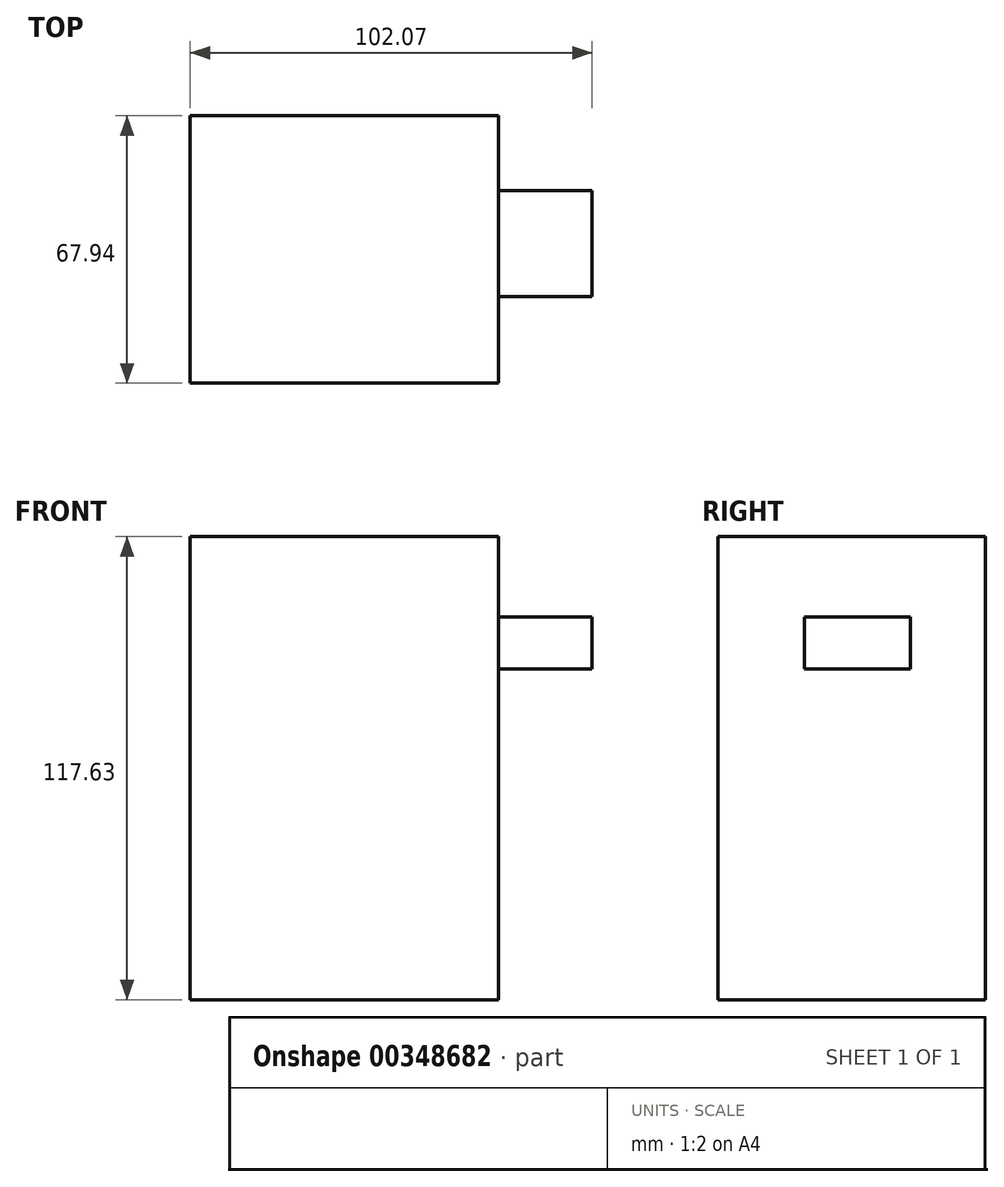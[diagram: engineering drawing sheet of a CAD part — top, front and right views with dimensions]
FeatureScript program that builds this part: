
annotation { "Feature Type Name" : "Feature", "Feature Type Description" : "" }
export const myFeature = defineFeature(function(context is Context, id is Id, definition is map)
    precondition{}
    {
        {
            var Q0;
            Q0=qCreatedBy(makeId("Top.planeOp"),FACE);
            var sketch = newSketch(context, id + "F0", { "sketchPlane" : qUnion([Q0])});
            skLineSegment(sketch, "E0.bottom", {"start": v(39.18, 45.93) * mm, "end": v(-39.18, 45.93) * mm});
            skLineSegment(sketch, "E0.top", {"start": v(39.18, -22.01) * mm, "end": v(-39.18, -22.01) * mm});
            skLineSegment(sketch, "E0.left", {"start": v(39.18, 45.93) * mm, "end": v(39.18, -22.01) * mm});
            skLineSegment(sketch, "E0.right", {"start": v(-39.18, 45.93) * mm, "end": v(-39.18, -22.01) * mm});
            skPoint(sketch, "E0.middle", {"position": v(0, 11.96) * mm});
            skSolve(sketch);
        }
        {
            var Q0;
            Q0=makeQuery(id+"F0.imprint","IMPRINT",FACE,{"disambiguationData":[TD([[makeQuery(id+"F0.imprint","IMPRINT",EDGE,{"derivedFrom":sQuery(id+"F0.wireOp",EDGE,"E0.bottom")}),1.0]])]});
            extrude(context, id + "F1", {"entities" : qUnion([Q0]), "depth" : 117.63 * mm});
        }
        {
            var Q0;
            Q0=makeQuery(id+"F1.opExtrude","SWEPT_FACE",FACE,{"disambiguationData":[OSD([sQuery(id+"F0.wireOp",EDGE,"E0.left")])]});
            var sketch = newSketch(context, id + "F2", { "sketchPlane" : qUnion([Q0])});
            skLineSegment(sketch, "E1.bottom", {"start": v(26.87, 97.23) * mm, "end": v(0, 97.23) * mm});
            skLineSegment(sketch, "E1.top", {"start": v(26.87, 83.97) * mm, "end": v(0, 83.97) * mm});
            skLineSegment(sketch, "E1.left", {"start": v(26.87, 97.23) * mm, "end": v(26.87, 83.97) * mm});
            skLineSegment(sketch, "E1.right", {"start": v(0, 97.23) * mm, "end": v(0, 83.97) * mm});
            skSolve(sketch);
        }
        {
            var Q0;
            Q0 = qSketchRegion(id + "F2", true);
            extrude(context, id + "F3", {"entities" : qUnion([Q0]), "operationType" : NewBodyOperationType.ADD, "depth" : 23.7 * mm});
        }
    });
